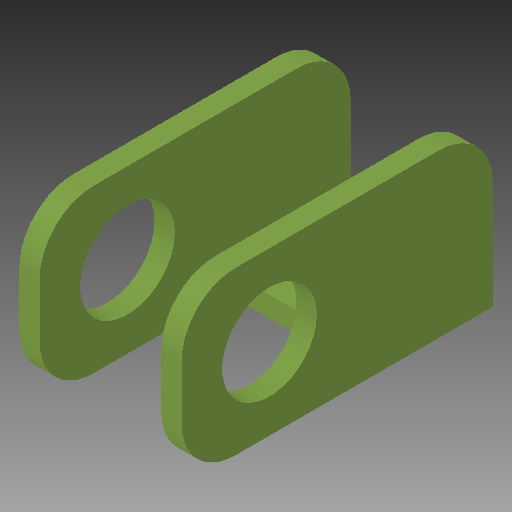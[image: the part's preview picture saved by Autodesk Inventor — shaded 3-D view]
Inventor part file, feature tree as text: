
AUTODESK INVENTOR PART (.ipt)
format: ipt  version: 2017 SP1 (Build 210196100, 196)  size: 161,280 bytes
history: native  units: in
note: dims shown in document units (in); Inventor stores cm internally (conversion verified against a paired STEP export)
features: extrude x3, sketch x3, fillet x1
ambient origin geometry x8: Origin, YZ Plane, XZ Plane, XY Plane, X Axis, Y Axis, Z Axis, Center Point
bodies: Solid1 (feature_tree)
feature tree (7):
  extrude  "Extrusion1"  Depth=1.5in
  extrude  "Extrusion2"  Depth=2.875in TaperAngle=0.0deg
  extrude  "Extrusion3"  Depth=0.75in
  fillet  "Fillet1"  Radius=0.75in
  sketch  "Sketch1"  dims[d0=0.1875in d2=1.5in]
  sketch  "Sketch2"  dims[d3=1.5in d4=2.875in d5=0.0in]
  sketch  "Sketch3"  dims[d6=0.2in d7=0.75in d8=0.75in d10=0.5625in d11=2.5in d12=0.0in d13=0.875in d14=0.75in d15=0.75in d16=1.6875in d17=2.5in d18=0.0in d19=0.5in d21=0.1875in d22=0.1875in]
